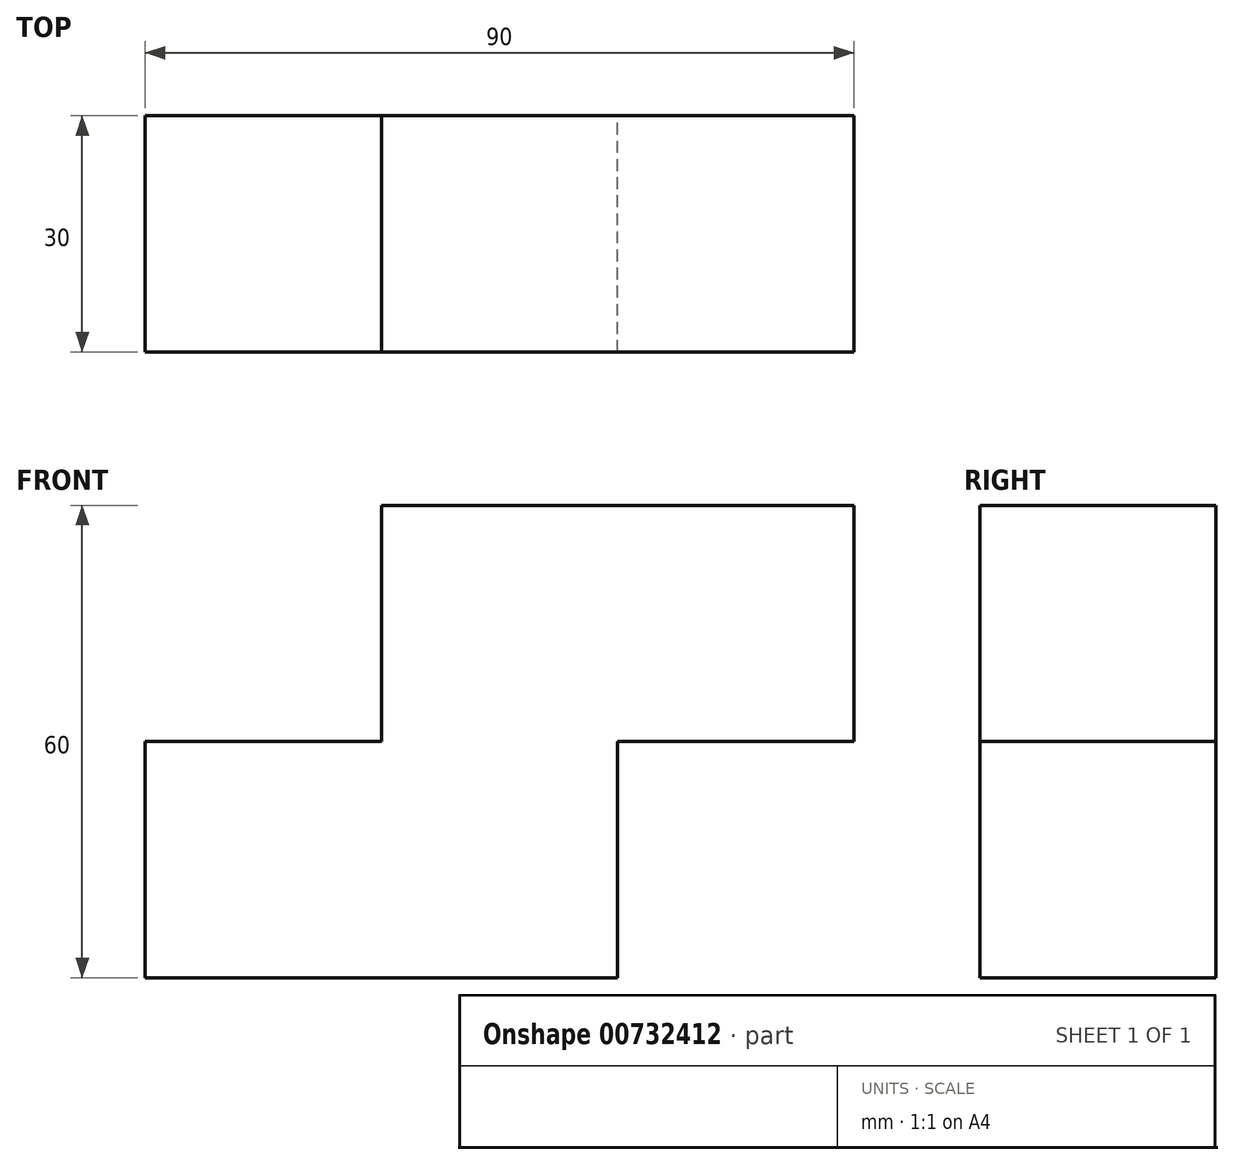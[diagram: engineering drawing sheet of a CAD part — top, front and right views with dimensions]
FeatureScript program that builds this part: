
annotation { "Feature Type Name" : "Feature", "Feature Type Description" : "" }
export const myFeature = defineFeature(function(context is Context, id is Id, definition is map)
    precondition{}
    {
        {
            var Q0;
            Q0=qCreatedBy(makeId("Front.planeOp"),FACE);
            var sketch = newSketch(context, id + "F0", { "sketchPlane" : qUnion([Q0])});
            skLineSegment(sketch, "E0", {"start": v(25.94, -51.95) * mm, "end": v(-34.06, -51.95) * mm});
            skLineSegment(sketch, "E1", {"start": v(-34.06, -51.95) * mm, "end": v(-34.06, -21.95) * mm});
            skLineSegment(sketch, "E2", {"start": v(-34.06, -21.95) * mm, "end": v(-4.06, -21.95) * mm});
            skLineSegment(sketch, "E3", {"start": v(-4.06, -21.95) * mm, "end": v(-4.06, 8.05) * mm});
            skLineSegment(sketch, "E4", {"start": v(-4.06, 8.05) * mm, "end": v(55.94, 8.05) * mm});
            skLineSegment(sketch, "E5", {"start": v(55.94, 8.05) * mm, "end": v(55.94, -21.95) * mm});
            skLineSegment(sketch, "E6", {"start": v(55.94, -21.95) * mm, "end": v(25.94, -21.95) * mm});
            skLineSegment(sketch, "E7", {"start": v(25.94, -21.95) * mm, "end": v(25.94, -51.95) * mm});
            skSolve(sketch);
        }
        {
            var Q0;
            Q0=makeQuery(id+"F0.imprint","IMPRINT",FACE,{"disambiguationData":[TD([[makeQuery(id+"F0.imprint","IMPRINT",EDGE,{"derivedFrom":sQuery(id+"F0.wireOp",EDGE,"E0")}),-1.0]])]});
            extrude(context, id + "F1", {"entities" : qUnion([Q0]), "depth" : 30 * mm, "offsetDistance" : 25 * mm});
        }
    });
